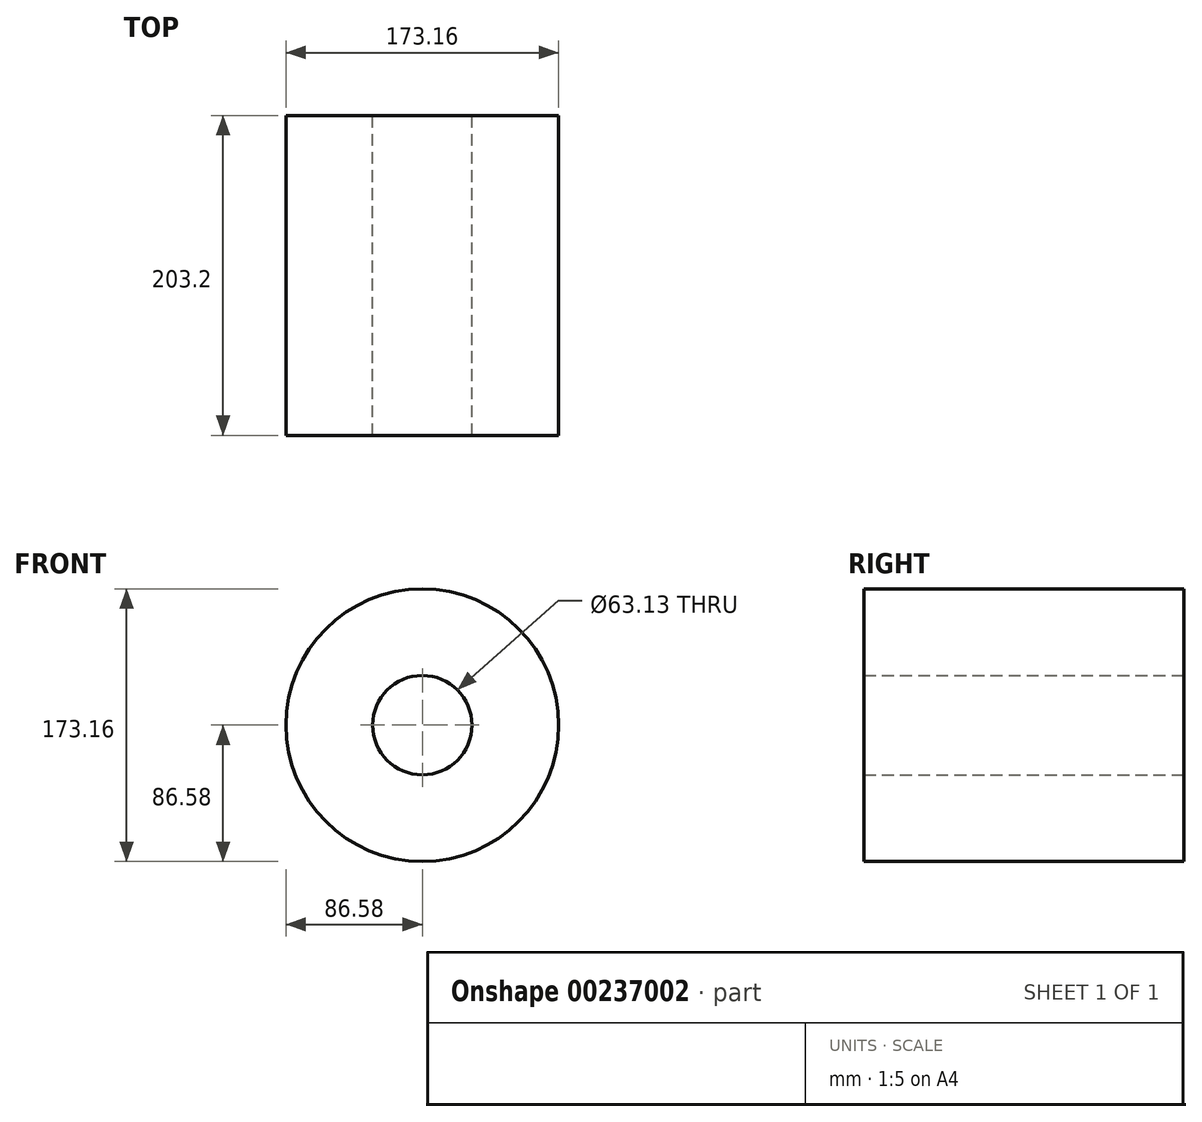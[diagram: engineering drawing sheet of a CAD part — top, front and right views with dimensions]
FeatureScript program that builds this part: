
annotation { "Feature Type Name" : "Feature", "Feature Type Description" : "" }
export const myFeature = defineFeature(function(context is Context, id is Id, definition is map)
    precondition{}
    {
        {
            var Q0;
            Q0=qCreatedBy(makeId("Front.planeOp"),FACE);
            var sketch = newSketch(context, id + "F0", { "sketchPlane" : qUnion([Q0])});
            skCircle(sketch, "E0", {"center": v(0, 0) * mm, "radius": 86.58 * mm});
            skCircle(sketch, "E1", {"center": v(0, 0) * mm, "radius": 31.56 * mm});
            skSolve(sketch);
        }
        {
            var Q0;
            Q0 = qSketchRegion(id + "F0", true);
            extrude(context, id + "F1", {"entities" : qUnion([Q0]), "depth" : 203.2 * mm});
        }
    });
